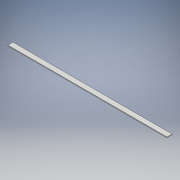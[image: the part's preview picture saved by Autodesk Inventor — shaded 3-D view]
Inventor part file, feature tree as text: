
AUTODESK INVENTOR PART (.ipt)
format: ipt  version: 2018 (Build 220112000, 112)  size: 93,184 bytes
history: native  units: mm
features: extrude x1, sketch x1
ambient origin geometry x8: Origin, YZ Plane, XZ Plane, XY Plane, X Axis, Y Axis, Z Axis, Center Point
bodies: Solid1 (feature_tree)
feature tree (2):
  extrude  "Extrusion1"  Depth=6.0mm
  sketch  "Sketch1"  dims[d0=38.1mm d1=6.0mm d2=1200.0mm d3=0.0mm]
